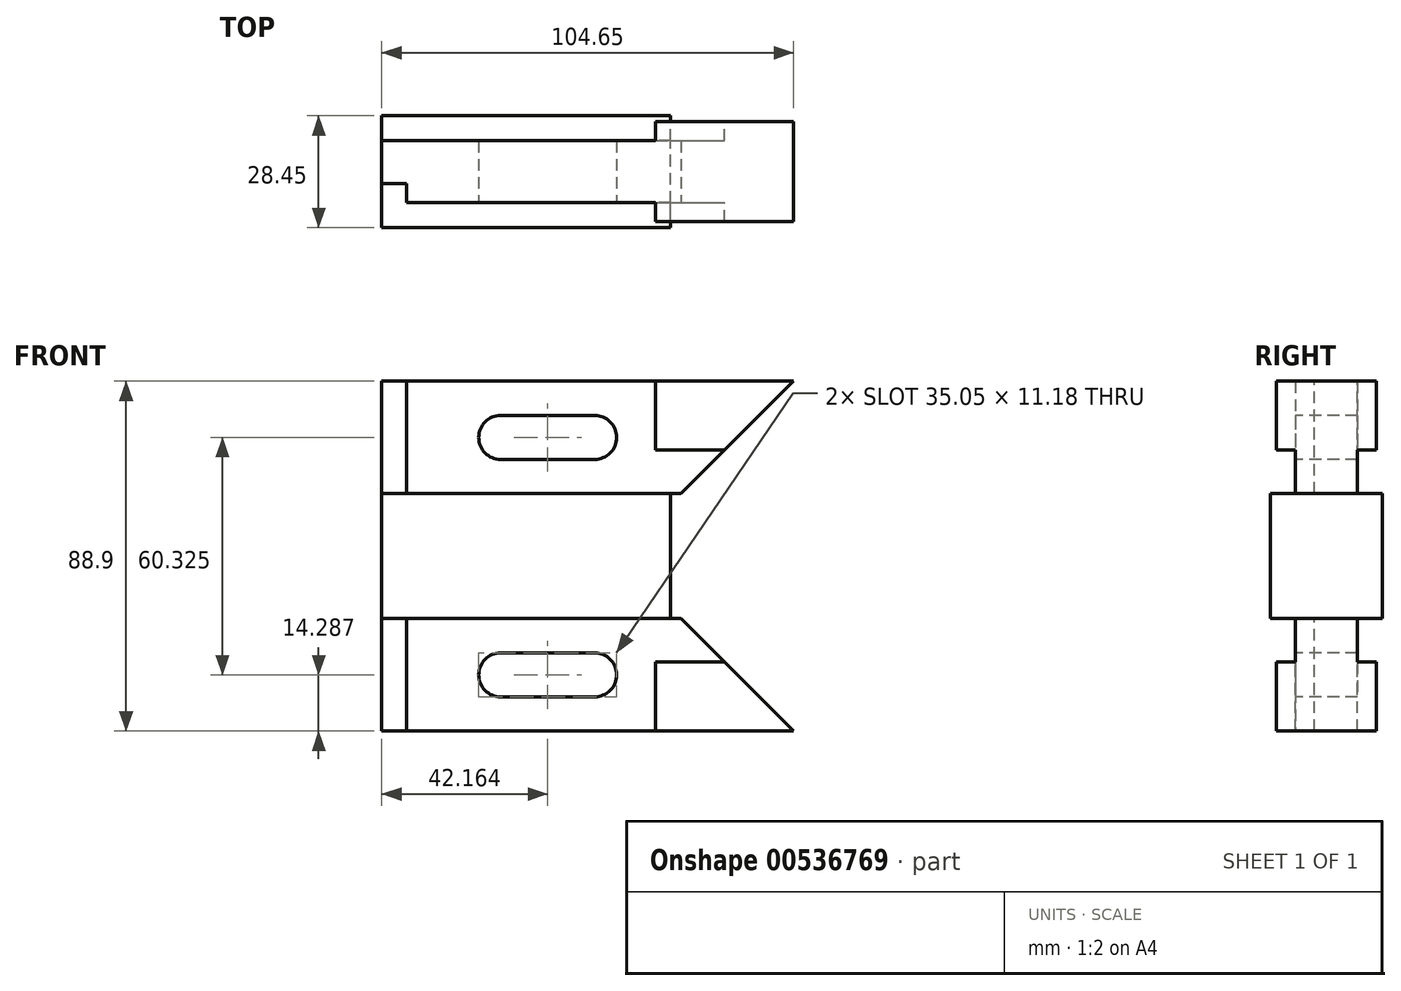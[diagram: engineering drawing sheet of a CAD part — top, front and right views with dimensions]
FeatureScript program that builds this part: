
annotation { "Feature Type Name" : "Feature", "Feature Type Description" : "" }
export const myFeature = defineFeature(function(context is Context, id is Id, definition is map)
    precondition{}
    {
        {
            var Q0;
            Q0=qCreatedBy(makeId("Front.planeOp"),FACE);
            var sketch = newSketch(context, id + "F0", { "sketchPlane" : qUnion([Q0])});
            skLineSegment(sketch, "E0", {"start": v(0, 0) * mm, "end": v(104.65, 0) * mm});
            skLineSegment(sketch, "E1", {"start": v(0, 0) * mm, "end": v(0, 28.58) * mm});
            skLineSegment(sketch, "E2", {"start": v(0, 28.58) * mm, "end": v(6.35, 28.58) * mm});
            skLineSegment(sketch, "E3", {"start": v(76.07, 28.58) * mm, "end": v(104.65, 0) * mm});
            skLineSegment(sketch, "E4", {"start": v(69.6, 0) * mm, "end": v(69.6, 17.53) * mm});
            skLineSegment(sketch, "E5", {"start": v(69.6, 17.53) * mm, "end": v(87.12, 17.53) * mm});
            skLineSegment(sketch, "E6", {"start": v(6.35, 28.58) * mm, "end": v(6.35, 0) * mm});
            skLineSegment(sketch, "E7", {"start": v(0, 14.29) * mm, "end": v(24.64, 14.29) * mm, "construction": true});
            skLineSegment(sketch, "E8.bottom", {"start": v(30.23, 8.7) * mm, "end": v(54.1, 8.7) * mm});
            skLineSegment(sketch, "E8.top", {"start": v(30.23, 19.88) * mm, "end": v(54.1, 19.88) * mm});
            skLineSegment(sketch, "E8.left", {"start": v(30.23, 8.7) * mm, "end": v(30.23, 19.88) * mm});
            skLineSegment(sketch, "E8.right", {"start": v(54.1, 8.7) * mm, "end": v(54.1, 19.88) * mm});
            skPoint(sketch, "E8.middle", {"position": v(42.16, 14.29) * mm});
            skArc(sketch, "E9", {"start": v(30.23, 19.88) * mm, "mid": v(24.64, 14.29) * mm, "end": v(30.23, 8.7) * mm});
            skArc(sketch, "E10", {"start": v(54.1, 8.7) * mm, "mid": v(59.7, 14.29) * mm, "end": v(54.1, 19.88) * mm});
            skLineSegment(sketch, "E11", {"start": v(0, 28.58) * mm, "end": v(0, 60.33) * mm});
            skLineSegment(sketch, "E12", {"start": v(0, 60.33) * mm, "end": v(0, 88.9) * mm});
            skLineSegment(sketch, "E13", {"start": v(0, 88.9) * mm, "end": v(104.65, 88.9) * mm});
            skLineSegment(sketch, "E14", {"start": v(104.65, 88.9) * mm, "end": v(76.07, 60.33) * mm});
            skLineSegment(sketch, "E15", {"start": v(76.07, 60.33) * mm, "end": v(6.35, 60.32) * mm});
            skLineSegment(sketch, "E16", {"start": v(6.35, 88.9) * mm, "end": v(6.35, 60.32) * mm});
            skLineSegment(sketch, "E17", {"start": v(6.35, 60.32) * mm, "end": v(0, 60.32) * mm});
            skLineSegment(sketch, "E18", {"start": v(6.35, 28.58) * mm, "end": v(76.07, 28.58) * mm});
            skLineSegment(sketch, "E19", {"start": v(0, 74.61) * mm, "end": v(24.64, 74.61) * mm, "construction": true});
            skLineSegment(sketch, "E20.bottom", {"start": v(30.23, 69.02) * mm, "end": v(54.1, 69.02) * mm});
            skLineSegment(sketch, "E20.top", {"start": v(30.23, 80.2) * mm, "end": v(54.1, 80.2) * mm});
            skLineSegment(sketch, "E20.left", {"start": v(30.23, 69.02) * mm, "end": v(30.23, 80.2) * mm});
            skLineSegment(sketch, "E20.right", {"start": v(54.1, 69.02) * mm, "end": v(54.1, 80.2) * mm});
            skPoint(sketch, "E20.middle", {"position": v(42.16, 74.61) * mm});
            skArc(sketch, "E21", {"start": v(30.23, 80.2) * mm, "mid": v(24.64, 74.61) * mm, "end": v(30.23, 69.02) * mm});
            skArc(sketch, "E22", {"start": v(54.1, 69.02) * mm, "mid": v(59.69, 74.61) * mm, "end": v(54.1, 80.2) * mm});
            skLineSegment(sketch, "E23", {"start": v(24.64, 74.61) * mm, "end": v(90.36, 74.61) * mm, "construction": true});
            skLineSegment(sketch, "E24", {"start": v(24.64, 14.29) * mm, "end": v(90.36, 14.29) * mm, "construction": true});
            skLineSegment(sketch, "E25", {"start": v(69.6, 88.9) * mm, "end": v(69.6, 71.37) * mm});
            skLineSegment(sketch, "E26", {"start": v(69.6, 71.37) * mm, "end": v(87.12, 71.37) * mm});
            skLineSegment(sketch, "E27", {"start": v(73.4, 60.33) * mm, "end": v(76.07, 60.33) * mm});
            skLineSegment(sketch, "E28", {"start": v(73.4, 60.33) * mm, "end": v(73.4, 28.58) * mm});
            skLineSegment(sketch, "E29", {"start": v(76.07, 28.58) * mm, "end": v(73.4, 28.58) * mm});
            skSolve(sketch);
        }
        {
            var Q0;
            Q0=makeQuery(id+"F0.imprint","IMPRINT",FACE,{"disambiguationData":[TD([[makeQuery(id+"F0.imprint","IMPRINT",EDGE,{"derivedFrom":sQuery(id+"F0.wireOp",EDGE,"E2")}),1.0]])]});
            extrude(context, id + "F1", {"entities" : qUnion([Q0]), "depth" : 6.35 * mm, "offsetDistance" : 25.4 * mm, "hasSecondDirection" : true, "secondDirectionOppositeDirection" : true, "secondDirectionDepth" : 22.1 * mm});
        }
        {
            var Q0;
            Q0=makeQuery(id+"F0.imprint","IMPRINT",FACE,{"disambiguationData":[TD([[makeQuery(id+"F0.imprint","IMPRINT",EDGE,{"derivedFrom":sQuery(id+"F0.wireOp",EDGE,"E15")}),-1.0]])]});
            var Q1;
            {var subQ0=sQuery(id+"F0.wireOp",EDGE,"E12");Q1=makeQuery(id+"F0.imprint","IMPRINT",FACE,{"disambiguationData":[TD([[makeQuery(id+"F0.imprint","IMPRINT",EDGE,{"derivedFrom":subQ0}),-1.0]])]});}
            var Q2;
            {var subQ0=sQuery(id+"F0.wireOp",EDGE,"E1");Q2=makeQuery(id+"F0.imprint","IMPRINT",FACE,{"disambiguationData":[TD([[makeQuery(id+"F0.imprint","IMPRINT",EDGE,{"derivedFrom":subQ0}),-1.0]])]});}
            var Q3;
            {var subQ2=sQuery(id+"F0.wireOp",EDGE,"E4");Q3=makeQuery(id+"F0.imprint","IMPRINT",FACE,{"disambiguationData":[TD([[makeQuery(id+"F0.imprint","IMPRINT",EDGE,{"derivedFrom":subQ2}),1.0]])]});}
            extrude(context, id + "F2", {"entities" : qUnion([Q0, Q1, Q2, Q3]), "operationType" : NewBodyOperationType.ADD, "oppositeDirection" : true, "depth" : 15.75 * mm, "offsetDistance" : 25.4 * mm});
        }
        {
            var Q0;
            {var subQ3=sQuery(id+"F0.wireOp",EDGE,"E25");Q0=makeQuery(id+"F0.imprint","IMPRINT",FACE,{"disambiguationData":[TD([[makeQuery(id+"F0.imprint","IMPRINT",EDGE,{"derivedFrom":subQ3}),1.0]])]});}
            var Q1;
            {var subQ3=sQuery(id+"F0.wireOp",EDGE,"E4");Q1=makeQuery(id+"F0.imprint","IMPRINT",FACE,{"disambiguationData":[TD([[makeQuery(id+"F0.imprint","IMPRINT",EDGE,{"derivedFrom":subQ3}),-1.0]])]});}
            extrude(context, id + "F3", {"entities" : qUnion([Q0, Q1]), "operationType" : NewBodyOperationType.ADD, "depth" : 4.83 * mm, "offsetDistance" : 25.4 * mm, "hasSecondDirection" : true, "secondDirectionOppositeDirection" : true, "secondDirectionDepth" : 20.57 * mm});
        }
        {
            var Q0;
            {var subQ0=sQuery(id+"F0.wireOp",EDGE,"E12");Q0=makeQuery(id+"F0.imprint","IMPRINT",FACE,{"disambiguationData":[TD([[makeQuery(id+"F0.imprint","IMPRINT",EDGE,{"derivedFrom":subQ0}),-1.0]])]});}
            var Q1;
            {var subQ0=sQuery(id+"F0.wireOp",EDGE,"E1");Q1=makeQuery(id+"F0.imprint","IMPRINT",FACE,{"disambiguationData":[TD([[makeQuery(id+"F0.imprint","IMPRINT",EDGE,{"derivedFrom":subQ0}),-1.0]])]});}
            extrude(context, id + "F4", {"entities" : qUnion([Q0, Q1]), "operationType" : NewBodyOperationType.REMOVE, "oppositeDirection" : true, "depth" : 4.83 * mm, "offsetDistance" : 25.4 * mm});
        }
    });
